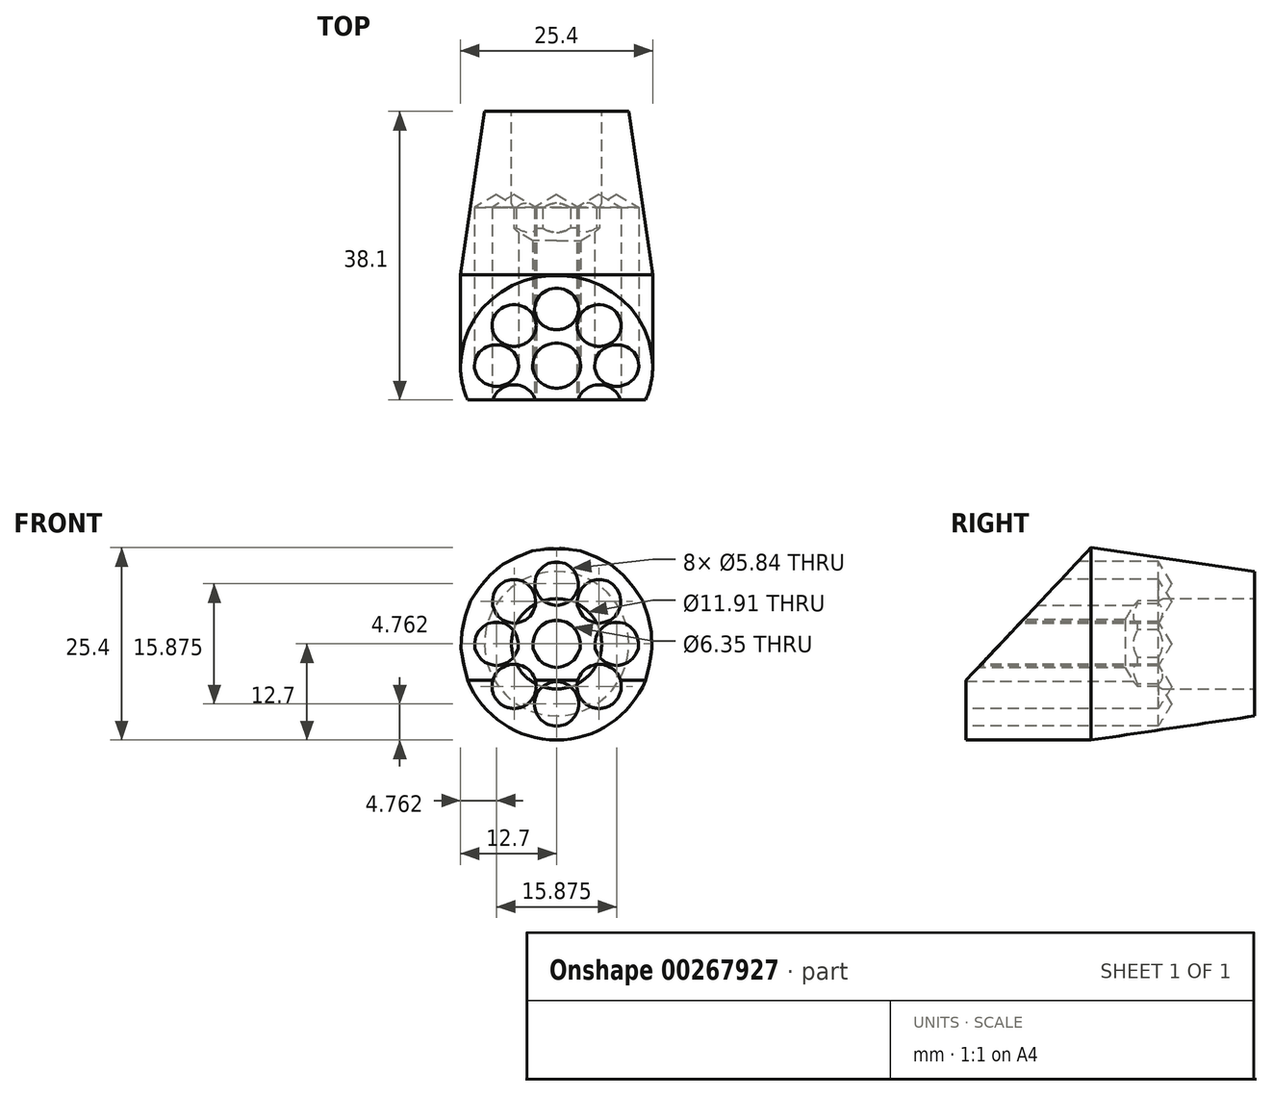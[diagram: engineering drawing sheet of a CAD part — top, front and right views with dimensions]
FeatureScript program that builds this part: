
annotation { "Feature Type Name" : "Feature", "Feature Type Description" : "" }
export const myFeature = defineFeature(function(context is Context, id is Id, definition is map)
    precondition{}
    {
        {
            var Q0;
            Q0=qCreatedBy(makeId("Front.planeOp"),FACE);
            var sketch = newSketch(context, id + "F0", { "sketchPlane" : qUnion([Q0])});
            skCircle(sketch, "E0", {"center": v(0, 0) * mm, "radius": 12.7 * mm});
            skSolve(sketch);
        }
        {
            var Q0;
            Q0=qSketchRegion(id+"F0",true);
            extrude(context, id + "F1", {"entities" : qUnion([Q0]), "depth" : 38.1 * mm});
        }
        {
            var Q0;
            Q0=makeQuery(id+"F1.opExtrude","CAP_FACE",FACE,{"disambiguationData":[OSD([sQuery(id+"F0.wireOp",EDGE,"E0")])],"isStart":true});
            var sketch = newSketch(context, id + "F2", { "sketchPlane" : qUnion([Q0])});
            skPoint(sketch, "E1", {"position": v(0, 0) * mm});
            skSolve(sketch);
        }
        {
            var Q0;
            Q0=sQuery(id+"F2.wireOp",VERTEX,"E1");
            var Q1;
            Q1=makeQuery(id+"F1.opExtrude","SWEPT_BODY",BODY,{"disambiguationData":[OSD([sQuery(id+"F0.wireOp",EDGE,"E0")])]});
            hole(context, id + "F3", {"style" : HoleStyle.SIMPLE, "endStyle" : HoleEndStyle.BLIND, "standardTappedOrClearance" : lookupTablePath({ "standard" : "ANSI", "engagement" : "75%", "pitch" : "28 tpi", "size" : "1/2", "type" : "Tapped" }), "standardBlindInLast" : lookupTablePath({ "standard" : "ANSI", "engagement" : "75%", "pitch" : "28 tpi", "size" : "1/2", "type" : "Tapped" }), "holeDiameter" : 11.9 * mm, "showTappedDepth" : true, "holeDepth" : 15.42 * mm, "tappedDepth" : 12.7 * mm, "tapClearance" : 3, "locations" : qUnion([Q0]), "scope" : qUnion([Q1]), "majorDiameter" : 12.7 * mm});
        }
        {
            var Q0;
            Q0=makeQuery(id+"F1.opExtrude","CAP_FACE",FACE,{"disambiguationData":[OSD([sQuery(id+"F0.wireOp",EDGE,"E0")])],"isStart":false});
            var sketch = newSketch(context, id + "F4", { "sketchPlane" : qUnion([Q0])});
            skPoint(sketch, "E2", {"position": v(0, 0) * mm});
            skSolve(sketch);
        }
        {
            var Q0;
            Q0=sQuery(id+"F4.wireOp",VERTEX,"E2");
            var Q1;
            Q1=makeQuery(id+"F1.opExtrude","SWEPT_BODY",BODY,{"disambiguationData":[OSD([sQuery(id+"F0.wireOp",EDGE,"E0")])]});
            hole(context, id + "F5", {"style" : HoleStyle.SIMPLE, "endStyle" : HoleEndStyle.THROUGH, "holeDiameter" : 6.35 * mm, "tappedDepth" : 12.7 * mm, "tapClearance" : 3, "locations" : qUnion([Q0]), "scope" : qUnion([Q1])});
        }
        {
            var Q0;
            Q0=makeQuery(id+"F1.opExtrude","CAP_FACE",FACE,{"disambiguationData":[OSD([sQuery(id+"F0.wireOp",EDGE,"E0")])],"isStart":false});
            var sketch = newSketch(context, id + "F6", { "sketchPlane" : qUnion([Q0])});
            skLineSegment(sketch, "E3", {"start": v(0, 3.18) * mm, "end": v(0, 12.7) * mm});
            skCircle(sketch, "E4.cCircle", {"center": v(0, 0) * mm, "radius": 7.94 * mm, "construction": true});
            skLineSegment(sketch, "E4.0", {"start": v(0, 7.94) * mm, "end": v(5.61, 5.61) * mm});
            skLineSegment(sketch, "E4.1", {"start": v(5.61, 5.61) * mm, "end": v(7.94, 0) * mm});
            skLineSegment(sketch, "E4.2", {"start": v(7.94, 0) * mm, "end": v(5.61, -5.61) * mm});
            skLineSegment(sketch, "E4.3", {"start": v(5.61, -5.61) * mm, "end": v(0, -7.94) * mm});
            skLineSegment(sketch, "E4.4", {"start": v(0, -7.94) * mm, "end": v(-5.61, -5.61) * mm});
            skLineSegment(sketch, "E4.5", {"start": v(-5.61, -5.61) * mm, "end": v(-7.94, 0) * mm});
            skLineSegment(sketch, "E4.6", {"start": v(-7.94, 0) * mm, "end": v(-5.61, 5.61) * mm});
            skLineSegment(sketch, "E4.7", {"start": v(-5.61, 5.61) * mm, "end": v(0, 7.94) * mm});
            skSolve(sketch);
        }
        {
            var Q0;
            Q0=sQuery(id+"F6.wireOp",VERTEX,"E4.7.end");
            var Q1;
            Q1=sQuery(id+"F6.wireOp",VERTEX,"E4.7.start");
            var Q2;
            Q2=sQuery(id+"F6.wireOp",VERTEX,"E4.6.start");
            var Q3;
            Q3=sQuery(id+"F6.wireOp",VERTEX,"E4.5.start");
            var Q4;
            Q4=sQuery(id+"F6.wireOp",VERTEX,"E4.4.start");
            var Q5;
            Q5=sQuery(id+"F6.wireOp",VERTEX,"E4.3.start");
            var Q6;
            Q6=sQuery(id+"F6.wireOp",VERTEX,"E4.2.start");
            var Q7;
            Q7=sQuery(id+"F6.wireOp",VERTEX,"E4.1.start");
            var Q8;
            Q8=makeQuery(id+"F1.opExtrude","SWEPT_BODY",BODY,{"disambiguationData":[OSD([sQuery(id+"F0.wireOp",EDGE,"E0")])]});
            hole(context, id + "F7", {"style" : HoleStyle.SIMPLE, "endStyle" : HoleEndStyle.BLIND, "holeDiameter" : 5.84 * mm, "holeDepth" : 25.4 * mm, "tappedDepth" : 12.7 * mm, "tapClearance" : 3, "locations" : qUnion([Q0, Q1, Q2, Q3, Q4, Q5, Q6, Q7]), "scope" : qUnion([Q8])});
        }
        {
            var Q0;
            Q0=makeQuery(id+"F1.opExtrude","CAP_FACE",FACE,{"disambiguationData":[OSD([sQuery(id+"F0.wireOp",EDGE,"E0")])],"isStart":false});
            var sketch = newSketch(context, id + "F8", { "sketchPlane" : qUnion([Q0])});
            skCircle(sketch, "E5.cCircle", {"center": v(0, 0) * mm, "radius": 12.7 * mm, "construction": true});
            skLineSegment(sketch, "E5.0", {"start": v(4.86, 11.73) * mm, "end": v(11.73, 4.86) * mm});
            skLineSegment(sketch, "E5.1", {"start": v(11.73, 4.86) * mm, "end": v(11.73, -4.86) * mm});
            skLineSegment(sketch, "E5.2", {"start": v(11.73, -4.86) * mm, "end": v(4.86, -11.73) * mm});
            skLineSegment(sketch, "E5.3", {"start": v(4.86, -11.73) * mm, "end": v(-4.86, -11.73) * mm});
            skLineSegment(sketch, "E5.4", {"start": v(-4.86, -11.73) * mm, "end": v(-11.73, -4.86) * mm});
            skLineSegment(sketch, "E5.5", {"start": v(-11.73, -4.86) * mm, "end": v(-11.73, 4.86) * mm});
            skLineSegment(sketch, "E5.6", {"start": v(-11.73, 4.86) * mm, "end": v(-4.86, 11.73) * mm});
            skLineSegment(sketch, "E5.7", {"start": v(-4.86, 11.73) * mm, "end": v(4.86, 11.73) * mm});
            skSolve(sketch);
        }
        {
            var Q0;
            Q0=makeQuery(id+"F1.opExtrude","CAP_FACE",FACE,{"disambiguationData":[OSD([sQuery(id+"F0.wireOp",EDGE,"E0")])],"isStart":false});
            var sketch = newSketch(context, id + "F9", { "sketchPlane" : qUnion([Q0])});
            skCircle(sketch, "E6", {"center": v(0, 0) * mm, "radius": 5.02 * mm});
            skSolve(sketch);
        }
        {
            var Q0;
            {var subQ2=sQuery(id+"F0.wireOp",EDGE,"E0");var subQ8=makeQuery(id+"F1.opExtrude","CAP_EDGE",EDGE,{"disambiguationData":[OSD([subQ2])],"isStart":false});Q0=makeQuery(id+"F9.imprint","IMPRINT",FACE,{"disambiguationData":[TD([[makeQuery(id+"F9.imprint","IMPRINT",EDGE,{"derivedFrom":makeQuery(id+"Fwdx6luw1CHeDt6_1.hole-1.boolean.opBoolean","SPLIT",EDGE,{"disambiguationData":[OD(1.0)],"derivedFrom":subQ8})}),1.0]])]});}
            cPlane(context, id + "F10", {"entities" : qUnion([Q0]), "cplaneType" : CPlaneType.OFFSET, "offset" : 12.7 * mm, "oppositeDirection" : true, "width" : 152.4 * mm, "height" : 152.4 * mm});
        }
        {
            var Q0;
            Q0=makeQuery(id+"F1.opExtrude","CAP_EDGE",EDGE,{"disambiguationData":[OSD([sQuery(id+"F0.wireOp",EDGE,"E0")])],"isStart":true});
            chamfer(context, id + "F11", {"entities" : qUnion([Q0]), "chamferType" : ChamferType.TWO_OFFSETS, "width1" : 21.59 * mm, "oppositeDirection" : false, "width2" : 3.17 * mm, "tangentPropagation" : true});
        }
        {
            var Q0;
            Q0=qCreatedBy(makeId("Right.planeOp"),FACE);
            var sketch = newSketch(context, id + "F12", { "sketchPlane" : qUnion([Q0])});
            skLineSegment(sketch, "E7", {"start": v(-38.16, -4.89) * mm, "end": v(-19.56, 14.86) * mm});
            skLineSegment(sketch, "E8", {"start": v(-19.56, 14.86) * mm, "end": v(-39.13, 17.54) * mm});
            skLineSegment(sketch, "E9", {"start": v(-39.13, 17.54) * mm, "end": v(-43.43, -3.89) * mm});
            skLineSegment(sketch, "E10", {"start": v(-43.43, -3.89) * mm, "end": v(-38.16, -4.89) * mm});
            skSolve(sketch);
        }
        {
            var Q0;
            Q0=makeQuery(id+"F12.imprint","IMPRINT",FACE,{"disambiguationData":[TD([[makeQuery(id+"F12.imprint","IMPRINT",EDGE,{"derivedFrom":sQuery(id+"F12.wireOp",EDGE,"E7")}),1.0]])]});
            extrude(context, id + "F13", {"entities" : qUnion([Q0]), "operationType" : NewBodyOperationType.REMOVE, "endBound" : BoundingType.SYMMETRIC, "oppositeDirection" : true, "depth" : 25.4 * mm});
        }
    });
